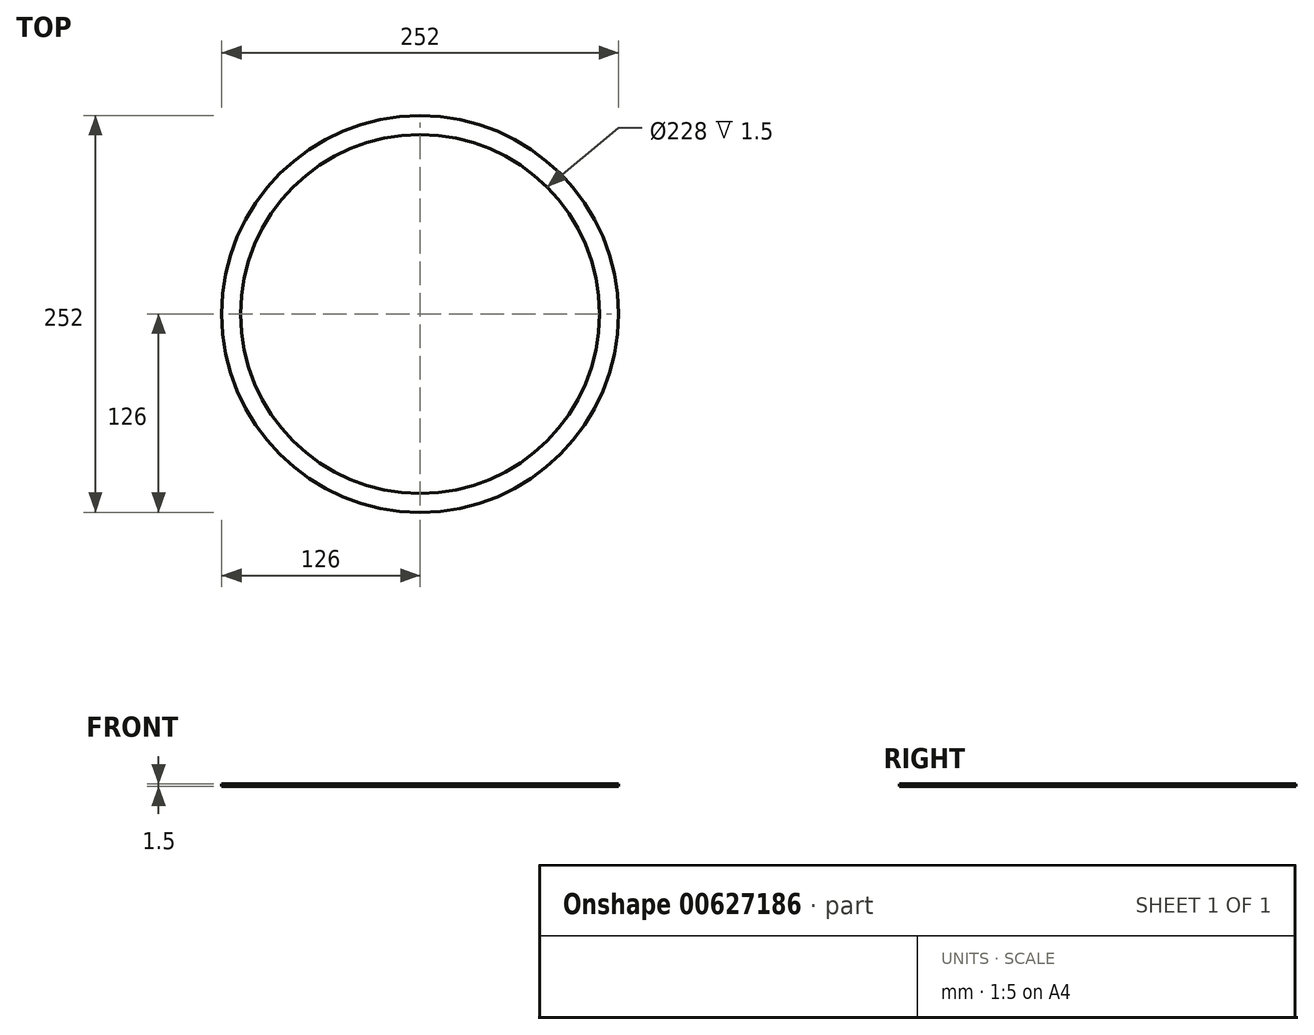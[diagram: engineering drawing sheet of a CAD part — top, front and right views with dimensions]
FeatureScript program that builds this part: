
annotation { "Feature Type Name" : "Feature", "Feature Type Description" : "" }
export const myFeature = defineFeature(function(context is Context, id is Id, definition is map)
    precondition{}
    {
        {
            var Q0;
            Q0=qCreatedBy(makeId("Top.planeOp"),FACE);
            var sketch = newSketch(context, id + "F0", { "sketchPlane" : qUnion([Q0])});
            skCircle(sketch, "E0", {"center": v(0, 0) * mm, "radius": 126 * mm});
            skCircle(sketch, "E1", {"center": v(0, 0) * mm, "radius": 114 * mm});
            skSolve(sketch);
        }
        {
            var Q0;
            Q0=makeQuery(id+"F0.imprint","IMPRINT",FACE,{"disambiguationData":[TD([[makeQuery(id+"F0.imprint","IMPRINT",EDGE,{"derivedFrom":sQuery(id+"F0.wireOp",EDGE,"E0")}),1.0]])]});
            extrude(context, id + "F1", {"entities" : qUnion([Q0]), "depth" : 1.5 * mm, "offsetDistance" : 25 * mm});
        }
    });
